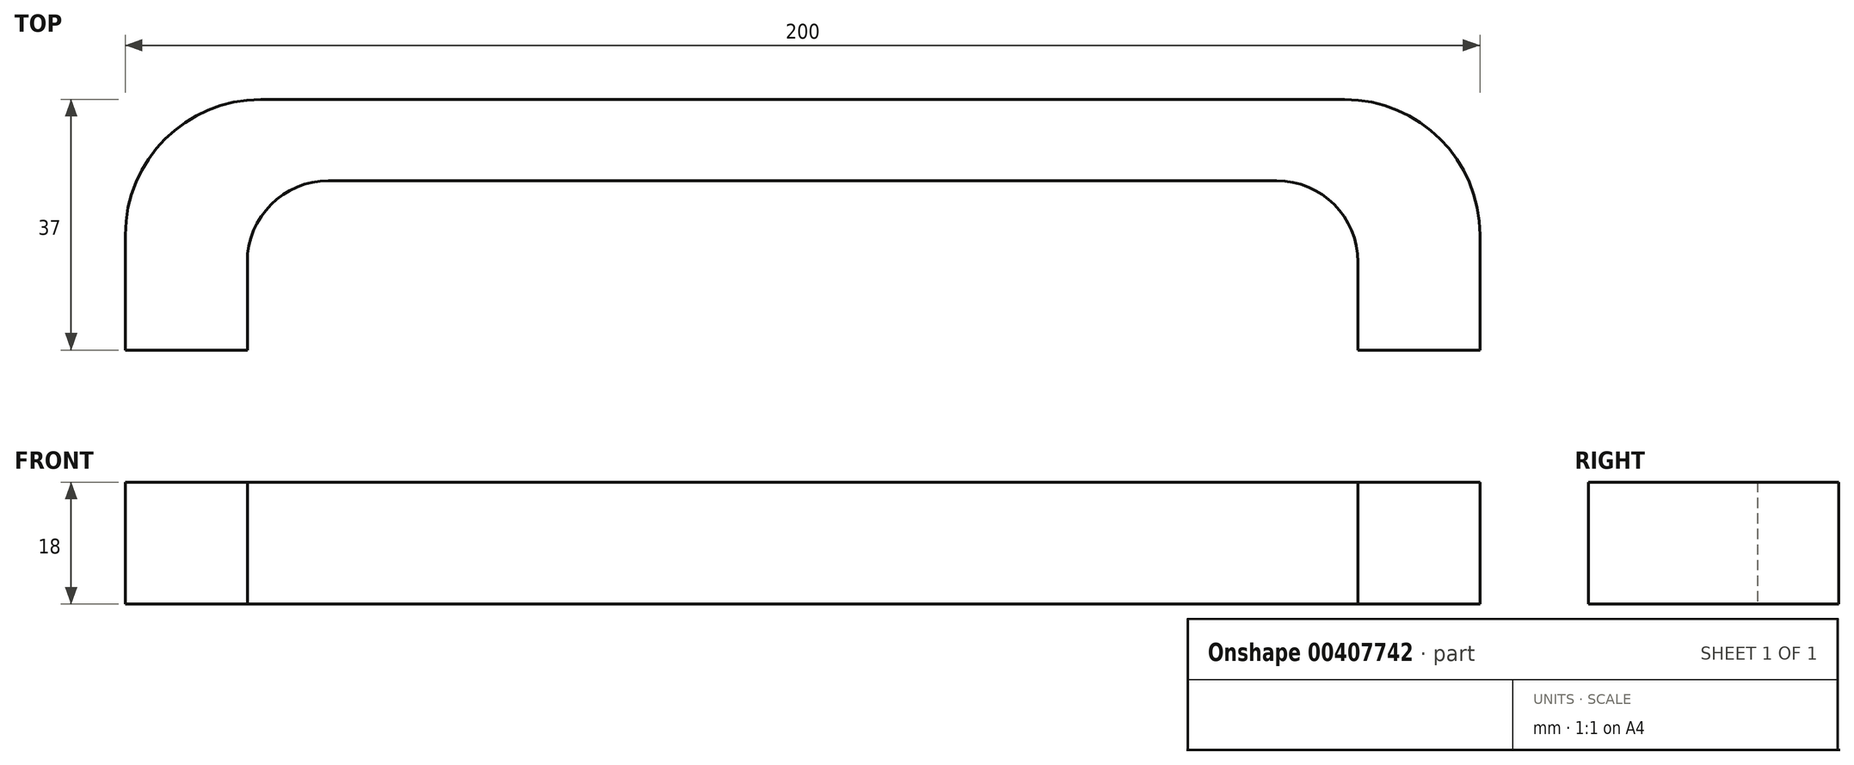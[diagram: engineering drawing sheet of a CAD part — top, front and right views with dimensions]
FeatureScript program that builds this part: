
annotation { "Feature Type Name" : "Feature", "Feature Type Description" : "" }
export const myFeature = defineFeature(function(context is Context, id is Id, definition is map)
    precondition{}
    {
        {
            var Q0;
            Q0=qCreatedBy(makeId("Top.planeOp"),FACE);
            var sketch = newSketch(context, id + "F0", { "sketchPlane" : qUnion([Q0])});
            skLineSegment(sketch, "E0", {"start": v(-100, 17) * mm, "end": v(-100, 0) * mm});
            skLineSegment(sketch, "E1", {"start": v(-100, 0) * mm, "end": v(-82, 0) * mm});
            skLineSegment(sketch, "E2", {"start": v(-82, 0) * mm, "end": v(-82, 13) * mm});
            skArc(sketch, "E3", {"start": v(-82, 13) * mm, "mid": v(-78.49, 21.49) * mm, "end": v(-70, 25) * mm});
            skArc(sketch, "E4", {"start": v(-100, 17) * mm, "mid": v(-94.14, 31.14) * mm, "end": v(-80, 37) * mm});
            skLineSegment(sketch, "E5.MirrorCS", {"start": v(100, 17) * mm, "end": v(100, 0) * mm});
            skArc(sketch, "E6.MirrorCS", {"start": v(100, 17) * mm, "mid": v(94.14, 31.14) * mm, "end": v(80, 37) * mm});
            skLineSegment(sketch, "E7.MirrorCS", {"start": v(100, 0) * mm, "end": v(82, 0) * mm});
            skLineSegment(sketch, "E8.MirrorCS", {"start": v(82, 0) * mm, "end": v(82, 13) * mm});
            skArc(sketch, "E9.MirrorCS", {"start": v(82, 13) * mm, "mid": v(78.49, 21.49) * mm, "end": v(70, 25) * mm});
            skLineSegment(sketch, "E10", {"start": v(-80, 37) * mm, "end": v(80, 37) * mm});
            skLineSegment(sketch, "E11", {"start": v(70, 25) * mm, "end": v(-70, 25) * mm});
            skSolve(sketch);
        }
        {
            var Q0;
            Q0 = qSketchRegion(id + "F0", true);
            extrude(context, id + "F1", {"entities" : qUnion([Q0]), "depth" : 18 * mm});
        }
    });
